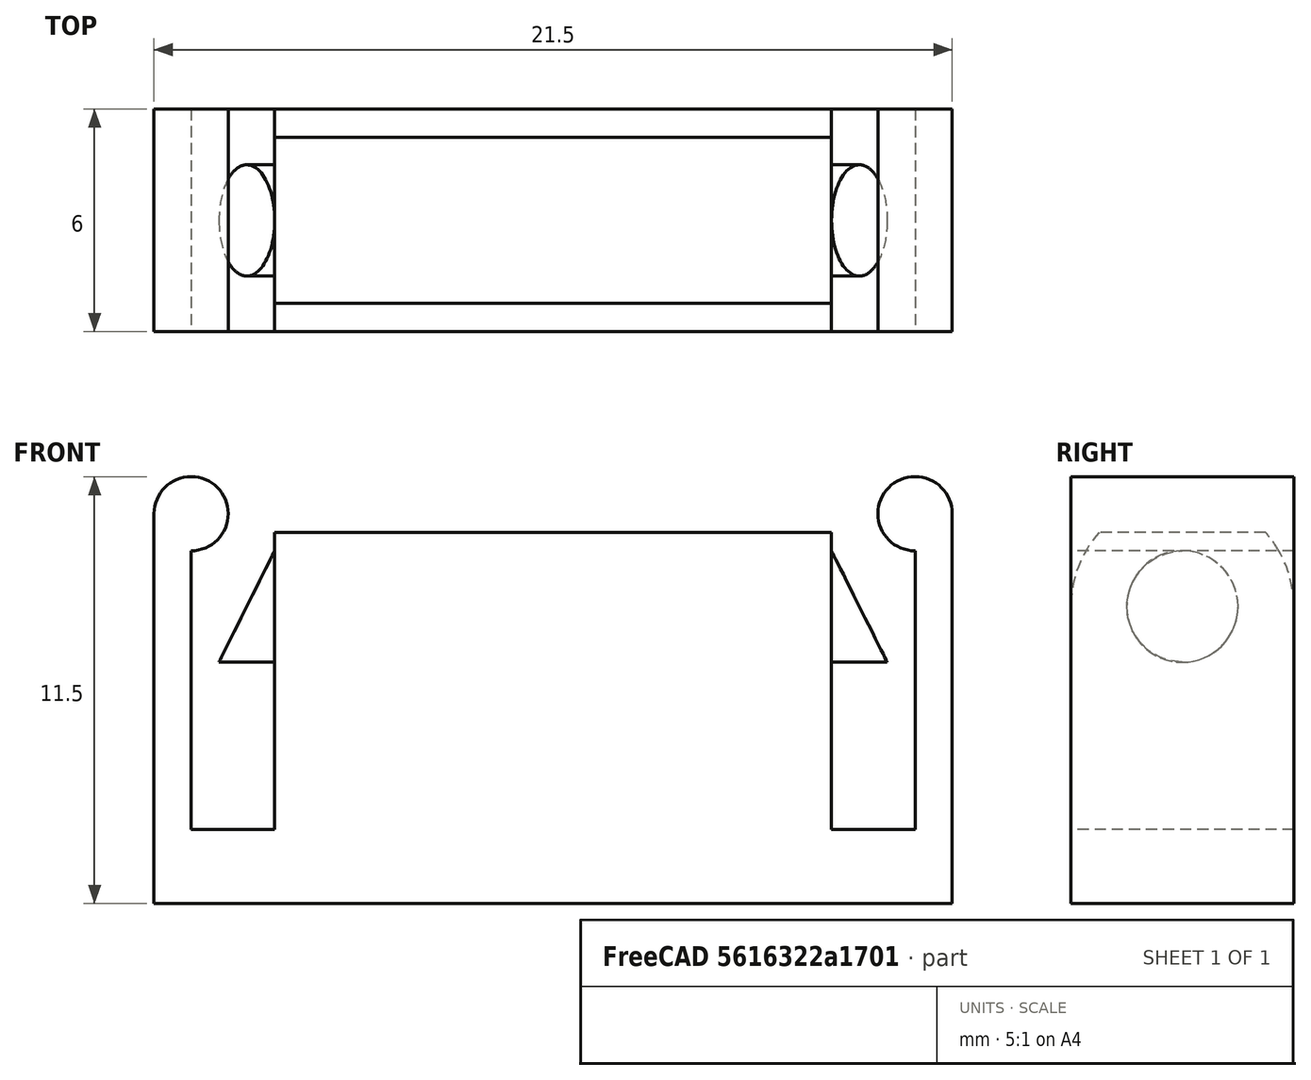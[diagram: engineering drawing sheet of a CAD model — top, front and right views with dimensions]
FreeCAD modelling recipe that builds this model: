
FCSTD DOCUMENT  (FreeCAD 1.0RUnknown)
Label: board_clamp
License: All rights reserved
LicenseURL: http://en.wikipedia.org/wiki/All_rights_reserved
objects: Sketcher::SketchObject×5, PartDesign::Pad×3, PartDesign::Pocket×2, PartDesign::Body×1, Mesh::Feature×1
note: 26 computed .brp shape members not serialized (recipe doc carries the construction recipe); baked Part::Feature solids carry a one-line shape summary decoded from their .brp

FEATURE [Sketcher::SketchObject] Sketch
  ArcFitTolerance = 1e-06
  AttachmentSupport = -> [XZ_Plane]
  FullyConstrained = true
  MakeInternals = false
  MapMode = 5
  Placement = pos=(0,0,0) rot=(1,0,0;1.5708rad)
  sketch-geometry (12):
    g0: LineSegment StartX=-10.75 StartY=0 StartZ=0 EndX=-10.75 EndY=10.5 EndZ=0
    g1: ArcOfCircle CenterX=-9.75 CenterY=10.5 CenterZ=0 NormalX=0 NormalY=0 NormalZ=1 AngleXU=0 Radius=1 StartAngle=4.71239 EndAngle=9.42478
    g2: LineSegment StartX=-9.75 StartY=9.5 StartZ=0 EndX=-9.75 EndY=2 EndZ=0
    g3: LineSegment StartX=-9.75 StartY=2 StartZ=0 EndX=-7.5 EndY=2 EndZ=0
    g4: LineSegment StartX=-7.5 StartY=2 StartZ=0 EndX=-7.5 EndY=10 EndZ=0
    g5: LineSegment StartX=-7.5 StartY=10 StartZ=0 EndX=7.5 EndY=10 EndZ=0
    g6: LineSegment StartX=7.5 StartY=10 StartZ=0 EndX=7.5 EndY=2 EndZ=0
    g7: LineSegment StartX=7.5 StartY=2 StartZ=0 EndX=9.75 EndY=2 EndZ=0
    g8: LineSegment StartX=9.75 StartY=2 StartZ=0 EndX=9.75 EndY=9.5 EndZ=0
    g9: LineSegment StartX=-10.75 StartY=0 StartZ=0 EndX=10.75 EndY=0 EndZ=0
    g10: LineSegment StartX=10.75 StartY=0 StartZ=0 EndX=10.75 EndY=10.5 EndZ=0
    g11: ArcOfCircle CenterX=9.75 CenterY=10.5 CenterZ=0 NormalX=0 NormalY=0 NormalZ=1 AngleXU=0 Radius=1 StartAngle=0 EndAngle=4.71239
  constraints (37):
    c: Vertical(g0)
    c: Coincident(g2,g1)
    c: Vertical(g2)
    c: Coincident(g3,g2)
    c: Horizontal(g3)
    c: Coincident(g4,g3)
    c: Vertical(g4)
    c: Horizontal(g5)
    c: Vertical(g6)
    c: Coincident(g7,g6)
    c: Horizontal(g7)
    c: Vertical(g8)
    c: Coincident(g9,g0)
    c: Horizontal(g9)
    c: Coincident(g10,g9)
    c: Vertical(g10)
    c: Coincident(g11,g8)
    c: Coincident(g11,g10)
    c: Distance(g3,g2) = 2.25
    c: Coincident(g7,g8)
    c: DistanceY(g4) = 10
    c: Coincident(g4,g5)
    c: Coincident(g5,g6)
    c: DistanceX(g4,g5) = 15
    c: Vertical(g8,g11)
    c: Symmetric(g9,g0,g-1)
    c: Horizontal(g3,g6)
    c: Radius(g11) = 1
    c: Horizontal(g11,g10)
    c: Radius(g1) = 1
    c: Horizontal(g0,g1)
    c: Vertical(g1,g1)
    c: Distance(g9,g3) = 2
    c: Coincident(g0,g1)
    c: Equal(g3,g7)
    c: DistanceY(g0,g0) = 10.5
    c: Horizontal(g1,g11)
FEATURE [PartDesign::Pad] Pad
  Direction = (0,-1,2e-16)
  Length = 6
  Length2 = 10
  Placement = pos=(0,0,0) rot=(1,0,0;1.5708rad)
  Profile = -> Sketch
  ReferenceAxis = -> Sketch [N_Axis]
  Suppressed = false
  Type = 0
FEATURE [Sketcher::SketchObject] Sketch002
  ArcFitTolerance = 1e-06
  AttachmentSupport = -> [Pad]
  FullyConstrained = true
  MakeInternals = false
  MapMode = 5
  Placement = pos=(7.5,0,0) rot=(0.707107,0,0.707107;3.14159rad)
  sketch-geometry (4):
    g0: ArcOfCircle CenterX=8 CenterY=3 CenterZ=0 NormalX=0 NormalY=0 NormalZ=1 AngleXU=0 Radius=3 StartAngle=4.71239 EndAngle=7.85398
    g1: LineSegment StartX=8 StartY=0 StartZ=0 EndX=11 EndY=0 EndZ=0
    g2: LineSegment StartX=11 StartY=0 StartZ=0 EndX=11 EndY=6 EndZ=0
    g3: LineSegment StartX=11 StartY=6 StartZ=0 EndX=8 EndY=6 EndZ=0
  constraints (11):
    c: Distance(g1) = 3
    c: Tangent(g1,g0) = -1.5708
    c: Horizontal(g1)
    c: Distance(g2) = 6
    c: Coincident(g2,g1)
    c: Vertical(g2)
    c: Tangent(g2,g0)
    c: Coincident(g3,g2)
    c: Tangent(g3,g0) = -1.5708
    c: DistanceX(g0) = 8
    c: DistanceY(g1) = 0
FEATURE [PartDesign::Pocket] Pocket
  BaseFeature = -> Pad
  Direction = (-1,0,2e-16)
  Length = 15
  Length2 = 5
  Placement = pos=(0,0,0) rot=(1,0,0;1.5708rad)
  Profile = -> Sketch002
  ReferenceAxis = -> Sketch002 [N_Axis]
  Suppressed = false
  Type = 0
FEATURE [Sketcher::SketchObject] Sketch004
  ArcFitTolerance = 1e-06
  FullyConstrained = true
  MakeInternals = false
  MapMode = 5
  Placement = pos=(-7.5,0,0) rot=(0.707107,0,-0.707107;3.14159rad)
  sketch-geometry (1):
    g0: Circle CenterX=-8 CenterY=3 CenterZ=0 NormalX=0 NormalY=0 NormalZ=1 AngleXU=0 Radius=1.5
  constraints (3):
    c: Diameter(g0) = 3
    c: DistanceY(g0) = 3
    c: DistanceX(g0) = -8
FEATURE [PartDesign::Pad] Pad001
  BaseFeature = -> Pocket
  Direction = (-1,-1e-16,-2e-16)
  Length = 1.5
  Length2 = 10
  Placement = pos=(0,0,0) rot=(1,0,0;1.5708rad)
  Profile = -> Sketch004
  ReferenceAxis = -> Sketch004 [N_Axis]
  Suppressed = false
  Type = 0
FEATURE [Sketcher::SketchObject] Sketch005
  ArcFitTolerance = 1e-06
  AttachmentSupport = -> [Pad001]
  FullyConstrained = true
  MakeInternals = false
  MapMode = 5
  Placement = pos=(7.5,0,0) rot=(0.707107,0,0.707107;3.14159rad)
  sketch-geometry (1):
    g0: Circle CenterX=8 CenterY=3 CenterZ=0 NormalX=0 NormalY=0 NormalZ=1 AngleXU=0 Radius=1.5
  constraints (3):
    c: Diameter(g0) = 3
    c: DistanceX(g0) = 8
    c: DistanceY(g0) = 3
FEATURE [PartDesign::Pad] Pad002
  BaseFeature = -> Pad001
  Direction = (1,0,-2e-16)
  Length = 1.5
  Length2 = 10
  Placement = pos=(0,0,0) rot=(1,0,0;1.5708rad)
  Profile = -> Sketch005 [Edge1]
  ReferenceAxis = -> Sketch005 [N_Axis]
  Suppressed = false
  Type = 0
FEATURE [Sketcher::SketchObject] Sketch006
  ArcFitTolerance = 1e-06
  AttachmentSupport = -> [Pad002]
  FullyConstrained = true
  MakeInternals = false
  MapMode = 5
  Placement = pos=(0,0,0) rot=(-1,0,0;1.5708rad)
  sketch-geometry (6):
    g0: LineSegment StartX=-7.5 StartY=-9.5 StartZ=0 EndX=-9 EndY=-9.5 EndZ=0
    g1: LineSegment StartX=-9 StartY=-9.5 StartZ=0 EndX=-9 EndY=-6.5 EndZ=0
    g2: LineSegment StartX=-9 StartY=-6.5 StartZ=0 EndX=-7.5 EndY=-9.5 EndZ=0
    g3: LineSegment StartX=7.5 StartY=-9.5 StartZ=0 EndX=9 EndY=-9.5 EndZ=0
    g4: LineSegment StartX=9 StartY=-9.5 StartZ=0 EndX=9 EndY=-6.5 EndZ=0
    g5: LineSegment StartX=9 StartY=-6.5 StartZ=0 EndX=7.5 EndY=-9.5 EndZ=0
  constraints (17):
    c: Horizontal(g0)
    c: Coincident(g1,g0)
    c: Vertical(g1)
    c: Coincident(g2,g1)
    c: Coincident(g2,g0)
    c: Horizontal(g3)
    c: Coincident(g4,g3)
    c: Vertical(g4)
    c: Coincident(g5,g4)
    c: Coincident(g5,g3)
    c: Equal(g0,g3)
    c: Equal(g4,g1)
    c: DistanceX(g0,g3) = 18
    c: DistanceY(g4,g-1) = 6.5
    c: Symmetric(g0,g3,g-2)
    c: DistanceX(g0,g0) = 1.5
    c: DistanceY(g1,g1) = 3
FEATURE [PartDesign::Pocket] Pocket001
  BaseFeature = -> Pad002
  Direction = (0,-1,-2e-16)
  Length = 5
  Length2 = 5
  Placement = pos=(0,0,0) rot=(1,0,0;1.5708rad)
  Profile = -> Sketch006
  ReferenceAxis = -> Sketch006 [N_Axis]
  Suppressed = false
  Type = 0
FEATURE [PartDesign::Body] Body  label="MB_mount"
  AllowCompound = false
  Group = -> [Sketch,Pad,Sketch002,Pocket,Sketch004,Pad001,Sketch005,Pad002,Sketch006,Pocket001]
  Origin = -> Origin
  Tip = -> Pocket001
FEATURE [Mesh::Feature] Mesh  label="MB_mount (Meshed)"
